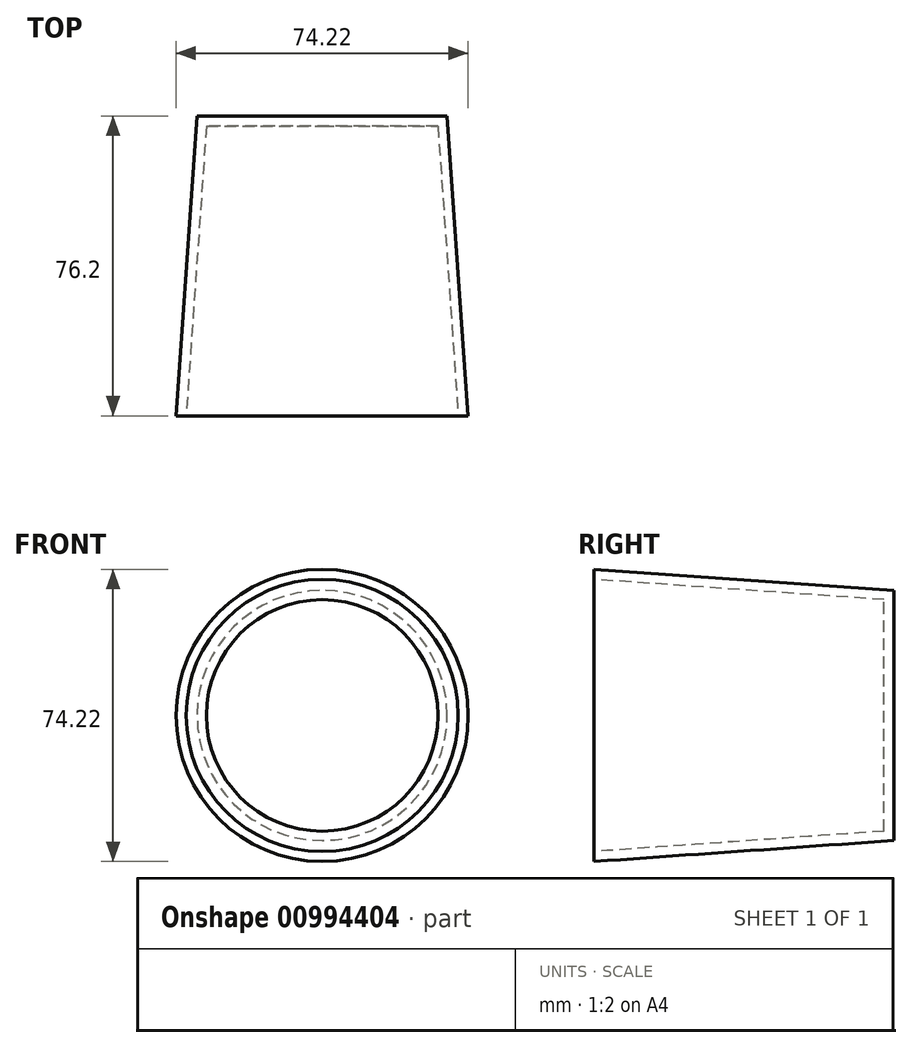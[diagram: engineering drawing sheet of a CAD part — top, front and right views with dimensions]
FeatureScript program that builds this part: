
annotation { "Feature Type Name" : "Feature", "Feature Type Description" : "" }
export const myFeature = defineFeature(function(context is Context, id is Id, definition is map)
    precondition{}
    {
        {
            var Q0;
            Q0=qCreatedBy(makeId("Front.planeOp"),FACE);
            var sketch = newSketch(context, id + "F0", { "sketchPlane" : qUnion([Q0])});
            skCircle(sketch, "E0", {"center": v(0, 0) * mm, "radius": 31.78 * mm});
            skSolve(sketch);
        }
        {
            var Q0;
            Q0=qCreatedBy(makeId("Front.planeOp"),FACE);
            var sketch = newSketch(context, id + "F1", { "sketchPlane" : qUnion([Q0])});
            skSolve(sketch);
        }
        {
            var Q0;
            Q0 = qSketchRegion(id + "F1", true);
            var Q1;
            Q1=makeQuery(id+"F0.imprint","IMPRINT",FACE,{"disambiguationData":[TD([[makeQuery(id+"F0.imprint","IMPRINT",EDGE,{"derivedFrom":sQuery(id+"F0.wireOp",EDGE,"E0")}),1.0]])]});
            extrude(context, id + "F2", {"entities" : qUnion([Q0, Q1]), "depth" : 76.2 * mm, "offsetDistance" : 25.4 * mm, "hasDraft" : true, "draftAngle" : 4 * degree});
        }
        {
            var Q0;
            Q0=makeQuery(id+"F2.opExtrude","CAP_FACE",FACE,{"disambiguationData":[OSD([sQuery(id+"F0.wireOp",EDGE,"E0")])],"isStart":false});
            shell(context, id + "F3", {"entities" : qUnion([Q0]), "thickness" : 2.54 * mm});
        }
    });
